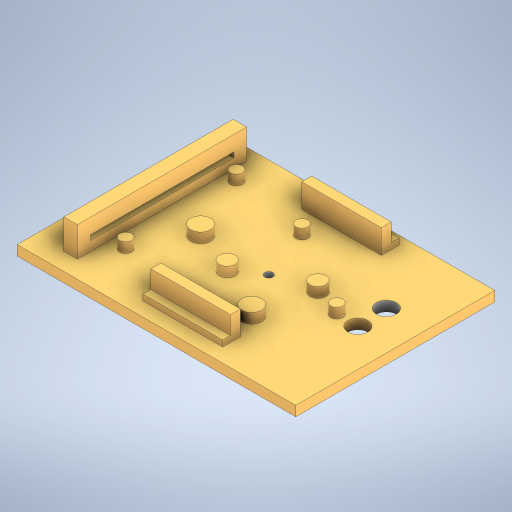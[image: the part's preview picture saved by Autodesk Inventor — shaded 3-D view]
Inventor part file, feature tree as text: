
AUTODESK INVENTOR PART (.ipt)
format: ipt  version: 2024 (Build 280153000, 153)  size: 390,656 bytes
history: native  units: mm
features: sketch x12, extrude x11, chamfer x1
ambient origin geometry x8: Origin, YZ Plane, XZ Plane, XY Plane, X Axis, Y Axis, Z Axis, Center Point
bodies: Solid1 (feature_tree)
feature tree (24):
  extrude  "Extrusion1"  Depth=100.0mm
  extrude  "Extrusion2"  Depth=5.0mm
  extrude  "Extrusion3"  Depth=10.0mm
  extrude  "Extrusion4"  Depth=8.0mm
  extrude  "Extrusion5"  Depth=5.0mm TaperAngle=0.0deg
  extrude  "Extrusion6"  Depth=8.0mm
  extrude  "Extrusion7"  Depth=85.0mm
  extrude  "Extrusion8"  Depth=21.5mm
  extrude  "Extrusion9"  Depth=4.85mm
  extrude  "Extrusion10"  Depth=72.0mm
  extrude  "Extrusion11"  Depth=40.0mm
  sketch  "Sketch12"  dims[d26=5.0mm d27=40.0mm d28=5.0mm d29=12.0mm d30=0.0mm d31=40.0mm d32=3.0mm d33=4.0mm d34=0.0mm d35=3.0mm d36=4.0mm d37=0.0mm d38=10.0mm d39=8.0mm d40=0.0mm d41=10.0mm d42=10.0mm d43=0.0mm d44=4.0mm d45=5.0mm d46=0.0mm d47=4.0mm d48=5.0mm d49=0.0mm d50=0.2mm d51=2.0mm d52=45.0deg]
  chamfer  "Chamfer1"  Distance=40.0mm
  sketch  "Sketch1"  dims[d0=140.0mm d1=100.0mm]
  sketch  "Sketch2"  dims[d2=5.0mm d3=0.0mm d4=6.0mm]
  sketch  "Sketch3"  dims[d5=6.0mm d6=10.0mm]
  sketch  "Sketch4"  dims[d7=6.0mm d8=8.0mm]
  sketch  "Sketch5"  dims[d9=10.0mm d10=5.0mm d11=0.0mm]
  sketch  "Sketch6"  dims[d12=8.0mm d13=6.0mm]
  sketch  "Sketch7"  dims[d14=7.0mm d15=85.0mm]
  sketch  "Sketch8"  dims[d16=15.0mm d17=0.0mm d18=21.5mm]
  sketch  "Sketch9"  dims[d19=2.5mm d20=4.85mm]
  sketch  "Sketch10"  dims[d21=2.5mm d22=0.0mm d23=72.0mm]
  sketch  "Sketch11"  dims[d24=6.5mm d25=40.0mm]
